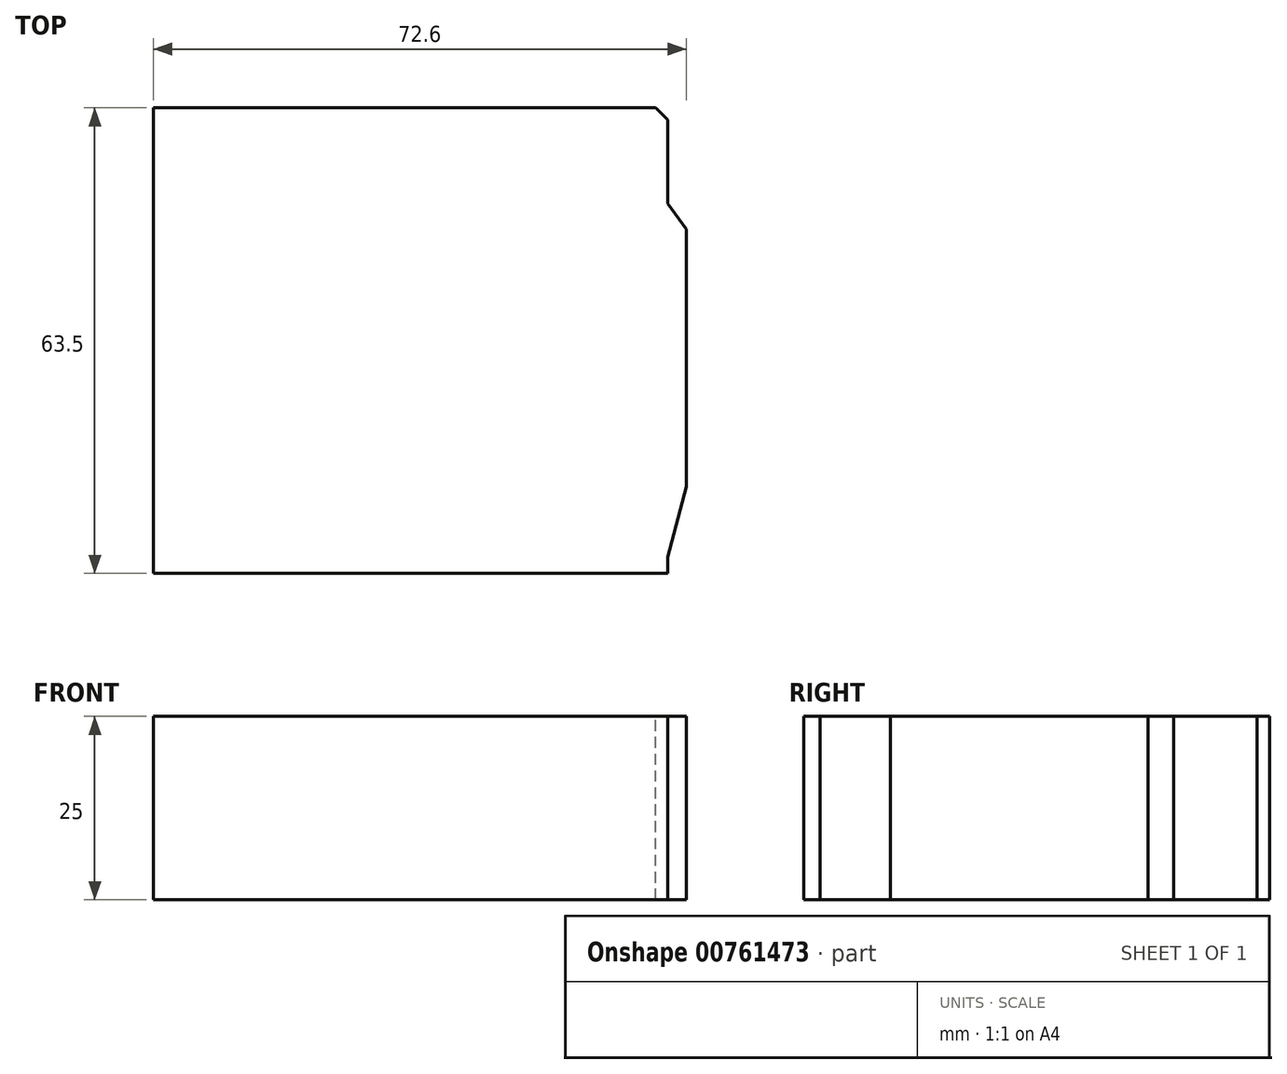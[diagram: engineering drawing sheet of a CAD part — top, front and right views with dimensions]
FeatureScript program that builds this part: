
annotation { "Feature Type Name" : "Feature", "Feature Type Description" : "" }
export const myFeature = defineFeature(function(context is Context, id is Id, definition is map)
    precondition{}
    {
        {
            var Q0;
            Q0=qCreatedBy(makeId("Top.planeOp"),FACE);
            var sketch = newSketch(context, id + "F0", { "sketchPlane" : qUnion([Q0])});
            skLineSegment(sketch, "E0.bottom", {"start": v(0, 0) * mm, "end": v(66.1, 0) * mm});
            skLineSegment(sketch, "E0.top", {"start": v(0, 59.5) * mm, "end": v(65.6, 59.5) * mm});
            skLineSegment(sketch, "E0.left", {"start": v(0, 0) * mm, "end": v(0, 59.5) * mm});
            skLineSegment(sketch, "E0.right", {"start": v(68.6, 10.1) * mm, "end": v(68.6, 44.3) * mm});
            skLineSegment(sketch, "E1", {"start": v(66.1, 59) * mm, "end": v(66.1, 47.8) * mm});
            skLineSegment(sketch, "E2", {"start": v(66.1, 47.8) * mm, "end": v(68.6, 44.3) * mm});
            skLineSegment(sketch, "E3", {"start": v(65.6, 59.5) * mm, "end": v(66.1, 59) * mm});
            skLineSegment(sketch, "E4", {"start": v(66.1, 0) * mm, "end": v(66.1, 0.5) * mm});
            skLineSegment(sketch, "E5", {"start": v(66.1, 0.5) * mm, "end": v(68.6, 10.1) * mm});
            skLineSegment(sketch, "E6.0", {"start": v(-2, -2) * mm, "end": v(-2, 61.5) * mm});
            skLineSegment(sketch, "E6.1", {"start": v(-2, -2) * mm, "end": v(68.1, -2) * mm});
            skLineSegment(sketch, "E6.2", {"start": v(-2, 61.5) * mm, "end": v(66.43, 61.5) * mm});
            skLineSegment(sketch, "E6.3", {"start": v(68.1, -2) * mm, "end": v(68.1, 0.24) * mm});
            skLineSegment(sketch, "E6.4", {"start": v(68.1, 0.24) * mm, "end": v(70.6, 9.84) * mm});
            skLineSegment(sketch, "E6.5", {"start": v(66.43, 61.5) * mm, "end": v(68.1, 59.83) * mm});
            skLineSegment(sketch, "E6.6", {"start": v(68.1, 59.83) * mm, "end": v(68.1, 48.44) * mm});
            skLineSegment(sketch, "E6.7", {"start": v(68.1, 48.44) * mm, "end": v(70.6, 44.94) * mm});
            skLineSegment(sketch, "E6.8", {"start": v(70.6, 9.84) * mm, "end": v(70.6, 44.94) * mm});
            skSolve(sketch);
        }
        {
            var Q0;
            Q0=sQuery(id+"F0.wireOp",EDGE,"E6.0");
            var Q1;
            Q1=sQuery(id+"F0.wireOp",EDGE,"E6.1");
            var Q2;
            Q2=sQuery(id+"F0.wireOp",EDGE,"E6.3");
            var Q3;
            Q3=sQuery(id+"F0.wireOp",EDGE,"E6.4");
            var Q4;
            Q4=sQuery(id+"F0.wireOp",EDGE,"E6.8");
            var Q5;
            Q5=sQuery(id+"F0.wireOp",EDGE,"E6.7");
            var Q6;
            Q6=sQuery(id+"F0.wireOp",EDGE,"E6.6");
            var Q7;
            Q7=sQuery(id+"F0.wireOp",EDGE,"E6.5");
            var Q8;
            Q8=sQuery(id+"F0.wireOp",EDGE,"E6.2");
            extrude(context, id + "F1", {"bodyType" : ToolBodyType.SURFACE, "surfaceEntities" : qUnion([Q0, Q1, Q2, Q3, Q4, Q5, Q6, Q7, Q8]), "depth" : 25 * mm, "offsetDistance" : 25 * mm});
        }
    });
